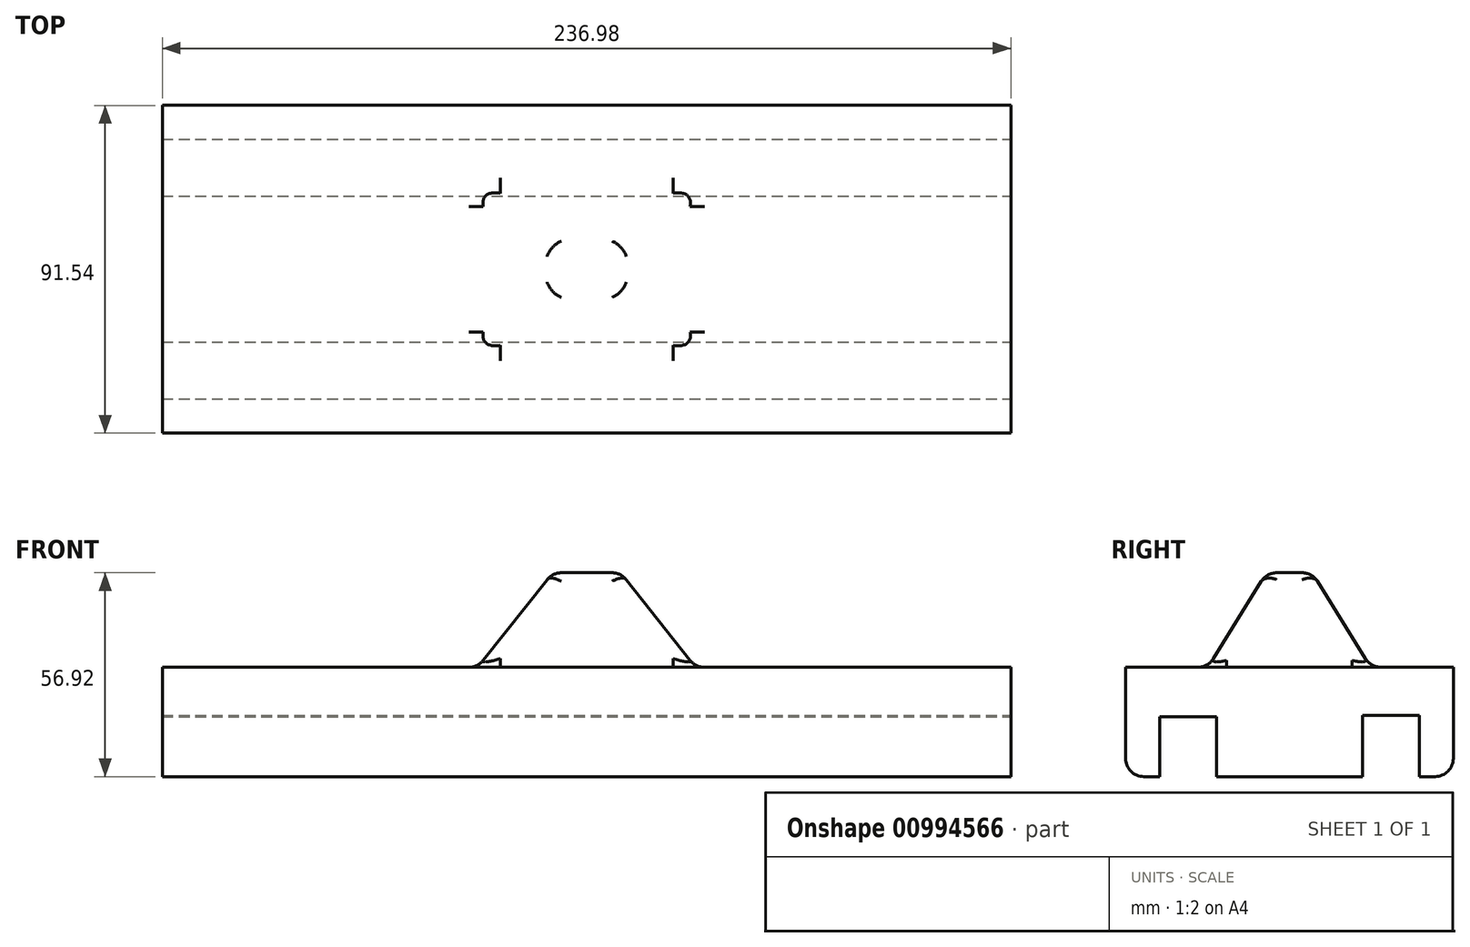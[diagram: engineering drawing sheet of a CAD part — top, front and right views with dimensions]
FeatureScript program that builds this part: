
annotation { "Feature Type Name" : "Feature", "Feature Type Description" : "" }
export const myFeature = defineFeature(function(context is Context, id is Id, definition is map)
    precondition{}
    {
        {
            var Q0;
            Q0=qCreatedBy(makeId("Front.planeOp"),FACE);
            var sketch = newSketch(context, id + "F0", { "sketchPlane" : qUnion([Q0])});
            skLineSegment(sketch, "E0.bottom", {"start": v(0, 0) * mm, "end": v(118.5, 0) * mm});
            skLineSegment(sketch, "E0.top", {"start": v(30.4, 30.53) * mm, "end": v(118.5, 30.53) * mm});
            skLineSegment(sketch, "E0.left", {"start": v(0, 0) * mm, "end": v(0, 30.53) * mm});
            skLineSegment(sketch, "E0.right", {"start": v(118.5, 0) * mm, "end": v(118.5, 30.53) * mm});
            skLineSegment(sketch, "E1", {"start": v(0, 30.53) * mm, "end": v(0, 56.92) * mm});
            skLineSegment(sketch, "E2", {"start": v(0, 56.92) * mm, "end": v(9.52, 56.92) * mm});
            skLineSegment(sketch, "E3", {"start": v(9.52, 56.92) * mm, "end": v(30.4, 30.53) * mm});
            skSolve(sketch);
        }
        {
            var Q0;
            Q0 = qSketchRegion(id + "F0", true);
            extrude(context, id + "F1", {"entities" : qUnion([Q0]), "depth" : 91.54 * mm, "offsetDistance" : 25.4 * mm, "symmetric" : true});
        }
        {
            var Q0;
            Q0=makeQuery(id+"F1.opExtrude","SWEPT_BODY",BODY,{"disambiguationData":[OSD([sQuery(id+"F0.wireOp",EDGE,"E0.bottom"),sQuery(id+"F0.wireOp",EDGE,"E0.top"),sQuery(id+"F0.wireOp",EDGE,"E0.left"),sQuery(id+"F0.wireOp",EDGE,"E0.right"),sQuery(id+"F0.wireOp",EDGE,"E1"),sQuery(id+"F0.wireOp",EDGE,"E2"),sQuery(id+"F0.wireOp",EDGE,"E3")])]});
            var Q1;
            Q1=makeQuery(id+"F1.opExtrude","SWEPT_FACE",FACE,{"disambiguationData":[OSD([sQuery(id+"F0.wireOp",EDGE,"E0.left"),sQuery(id+"F0.wireOp",EDGE,"E1")])]});
            mirror(context, id + "F2", {"operationType" : NewBodyOperationType.ADD, "entities" : qUnion([Q0]), "mirrorPlane" : qUnion([Q1])});
        }
        {
            var Q0;
            Q0=makeQuery(id+"F1.opExtrude","SWEPT_FACE",FACE,{"disambiguationData":[OSD([sQuery(id+"F0.wireOp",EDGE,"E0.right")])]});
            var sketch = newSketch(context, id + "F3", { "sketchPlane" : qUnion([Q0])});
            skLineSegment(sketch, "E4", {"start": v(0, 56.58) * mm, "end": v(0, 30.53) * mm});
            skLineSegment(sketch, "E5", {"start": v(22.72, 30.53) * mm, "end": v(6.35, 56.92) * mm});
            skLineSegment(sketch, "E6", {"start": v(6.35, 56.92) * mm, "end": v(45.77, 56.92) * mm});
            skLineSegment(sketch, "E7", {"start": v(45.77, 56.92) * mm, "end": v(45.77, 30.53) * mm});
            skLineSegment(sketch, "E8", {"start": v(45.77, 30.53) * mm, "end": v(22.72, 30.53) * mm});
            skLineSegment(sketch, "E9.MirrorCS", {"start": v(-45.77, 30.53) * mm, "end": v(-22.72, 30.53) * mm});
            skLineSegment(sketch, "E10.MirrorCS", {"start": v(-6.35, 56.92) * mm, "end": v(-45.77, 56.92) * mm});
            skLineSegment(sketch, "E11.MirrorCS", {"start": v(-22.72, 30.53) * mm, "end": v(-6.35, 56.92) * mm});
            skLineSegment(sketch, "E12.MirrorCS", {"start": v(-45.77, 56.92) * mm, "end": v(-45.77, 30.53) * mm});
            skSolve(sketch);
        }
        {
            var Q0;
            Q0 = qSketchRegion(id + "F3", true);
            extrude(context, id + "F4", {"entities" : qUnion([Q0]), "operationType" : NewBodyOperationType.REMOVE, "endBound" : BoundingType.THROUGH_ALL, "oppositeDirection" : true, "depth" : 25.4 * mm, "offsetDistance" : 25.4 * mm});
        }
        {
            var Q0;
            Q0=makeQuery(id+"F1.opExtrude","SWEPT_FACE",FACE,{"disambiguationData":[OSD([sQuery(id+"F0.wireOp",EDGE,"E0.right")])]});
            var sketch = newSketch(context, id + "F5", { "sketchPlane" : qUnion([Q0])});
            skLineSegment(sketch, "E13.bottom", {"start": v(-36.25, 0) * mm, "end": v(-20.37, 0) * mm});
            skLineSegment(sketch, "E13.top", {"start": v(-36.25, 16.66) * mm, "end": v(-20.37, 16.66) * mm});
            skLineSegment(sketch, "E13.left", {"start": v(-36.25, 0) * mm, "end": v(-36.25, 16.66) * mm});
            skLineSegment(sketch, "E13.right", {"start": v(-20.37, 0) * mm, "end": v(-20.37, 16.66) * mm});
            skSolve(sketch);
        }
        {
            var Q0;
            Q0 = qSketchRegion(id + "F5", true);
            extrude(context, id + "F6", {"entities" : qUnion([Q0]), "operationType" : NewBodyOperationType.REMOVE, "endBound" : BoundingType.UP_TO_NEXT, "oppositeDirection" : true, "depth" : 116.33 * mm, "offsetDistance" : 25.4 * mm, "hasSecondDirection" : true, "secondDirectionOppositeDirection" : false, "secondDirectionDepth" : 25.4 * mm});
        }
        {
            var Q0;
            Q0=makeQuery(id+"F1.opExtrude","SWEPT_FACE",FACE,{"disambiguationData":[OSD([sQuery(id+"F0.wireOp",EDGE,"E0.right")])]});
            var sketch = newSketch(context, id + "F7", { "sketchPlane" : qUnion([Q0])});
            skLineSegment(sketch, "E14.bottom", {"start": v(36.25, 0) * mm, "end": v(20.37, 0) * mm});
            skLineSegment(sketch, "E14.top", {"start": v(36.25, 17.1) * mm, "end": v(20.37, 17.1) * mm});
            skLineSegment(sketch, "E14.left", {"start": v(36.25, 0) * mm, "end": v(36.25, 17.1) * mm});
            skLineSegment(sketch, "E14.right", {"start": v(20.37, 0) * mm, "end": v(20.37, 17.1) * mm});
            skSolve(sketch);
        }
        {
            var Q0;
            Q0 = qSketchRegion(id + "F7", true);
            extrude(context, id + "F8", {"entities" : qUnion([Q0]), "operationType" : NewBodyOperationType.REMOVE, "endBound" : BoundingType.UP_TO_NEXT, "oppositeDirection" : true, "depth" : 25.4 * mm, "offsetDistance" : 25.4 * mm});
        }
        {
            var Q0;
            {var subQ0=makeQuery(id+"F1.opExtrude","SWEPT_FACE",FACE,{"disambiguationData":[OSD([sQuery(id+"F0.wireOp",EDGE,"E2")])]});Q0=makeQuery(id+"F2.boolean.opBoolean","MERGE",FACE,{"derivedFrom":[subQ0,makeQuery(id+"F2.opPattern","COPY",FACE,{"derivedFrom":subQ0,"instanceName":"1"})]});}
            fillet(context, id + "F9", {"entities" : qUnion([Q0]), "radius" : 5.08 * mm, "tangentPropagation" : true, "allowEdgeOverflow" : false});
        }
        {
            var Q0;
            {var subQ0=makeQuery(id+"F1.opExtrude","CAP_EDGE",EDGE,{"disambiguationData":[OSD([sQuery(id+"F0.wireOp",EDGE,"E0.bottom")])],"isStart":true});Q0=makeQuery(id+"F2.boolean.opBoolean","MERGE",EDGE,{"derivedFrom":[subQ0,makeQuery(id+"F2.opPattern","COPY",EDGE,{"derivedFrom":subQ0,"instanceName":"1"})]});}
            var Q1;
            {var subQ0=makeQuery(id+"F1.opExtrude","CAP_EDGE",EDGE,{"disambiguationData":[OSD([sQuery(id+"F0.wireOp",EDGE,"E0.bottom")])],"isStart":false});Q1=makeQuery(id+"F2.boolean.opBoolean","MERGE",EDGE,{"derivedFrom":[subQ0,makeQuery(id+"F2.opPattern","COPY",EDGE,{"derivedFrom":subQ0,"instanceName":"1"})]});}
            fillet(context, id + "F10", {"entities" : qUnion([Q0, Q1]), "radius" : 5.08 * mm, "tangentPropagation" : true, "allowEdgeOverflow" : false});
        }
        {
            var Q0;
            Q0=makeQuery(id+"F1.opExtrude","SWEPT_EDGE",EDGE,{"disambiguationData":[OSD([sQuery(id+"F0.wireOp",EDGE,"E0.top"),sQuery(id+"F0.wireOp",EDGE,"E3")])]});
            var Q1;
            Q1=makeQuery(id+"F4.boolean.opBoolean","INTERSECT",EDGE,{"derivedFrom":[makeQuery(id+"F1.opExtrude","SWEPT_FACE",FACE,{"disambiguationData":[OSD([sQuery(id+"F0.wireOp",EDGE,"E3")])]}),makeQuery(id+"F4.opExtrude","SWEPT_FACE",FACE,{"disambiguationData":[OSD([sQuery(id+"F3.wireOp",EDGE,"E11.MirrorCS")])]})]});
            var Q2;
            Q2=makeQuery(id+"F4.boolean.opBoolean","COPY",EDGE,{"derivedFrom":makeQuery(id+"F4.opExtrude","SWEPT_EDGE",EDGE,{"disambiguationData":[OSD([sQuery(id+"F0.wireOp",EDGE,"E0.top"),sQuery(id+"F0.wireOp",EDGE,"E0.right"),sQuery(id+"F3.wireOp",EDGE,"E9.MirrorCS"),sQuery(id+"F3.wireOp",EDGE,"E11.MirrorCS")])]})});
            var Q3;
            Q3=makeQuery(id+"F4.boolean.opBoolean","INTERSECT",EDGE,{"derivedFrom":[makeQuery(id+"F1.opExtrude","SWEPT_FACE",FACE,{"disambiguationData":[OSD([sQuery(id+"F0.wireOp",EDGE,"E3")])]}),makeQuery(id+"F4.opExtrude","SWEPT_FACE",FACE,{"disambiguationData":[OSD([sQuery(id+"F3.wireOp",EDGE,"E5")])]})]});
            var Q4;
            Q4=makeQuery(id+"F4.boolean.opBoolean","INTERSECT",EDGE,{"derivedFrom":[makeQuery(id+"F2.opPattern","COPY",FACE,{"derivedFrom":makeQuery(id+"F1.opExtrude","SWEPT_FACE",FACE,{"disambiguationData":[OSD([sQuery(id+"F0.wireOp",EDGE,"E3")])]}),"instanceName":"1"}),makeQuery(id+"F4.opExtrude","SWEPT_FACE",FACE,{"disambiguationData":[OSD([sQuery(id+"F3.wireOp",EDGE,"E11.MirrorCS")])]})]});
            var Q5;
            Q5=makeQuery(id+"F2.opPattern","COPY",EDGE,{"derivedFrom":makeQuery(id+"F1.opExtrude","SWEPT_EDGE",EDGE,{"disambiguationData":[OSD([sQuery(id+"F0.wireOp",EDGE,"E0.top"),sQuery(id+"F0.wireOp",EDGE,"E3")])]}),"instanceName":"1"});
            var Q6;
            Q6=makeQuery(id+"F4.boolean.opBoolean","INTERSECT",EDGE,{"derivedFrom":[makeQuery(id+"F2.opPattern","COPY",FACE,{"derivedFrom":makeQuery(id+"F1.opExtrude","SWEPT_FACE",FACE,{"disambiguationData":[OSD([sQuery(id+"F0.wireOp",EDGE,"E3")])]}),"instanceName":"1"}),makeQuery(id+"F4.opExtrude","SWEPT_FACE",FACE,{"disambiguationData":[OSD([sQuery(id+"F3.wireOp",EDGE,"E5")])]})]});
            var Q7;
            Q7=makeQuery(id+"F4.boolean.opBoolean","COPY",EDGE,{"derivedFrom":makeQuery(id+"F4.opExtrude","SWEPT_EDGE",EDGE,{"disambiguationData":[OSD([sQuery(id+"F0.wireOp",EDGE,"E0.top"),sQuery(id+"F0.wireOp",EDGE,"E0.right"),sQuery(id+"F3.wireOp",EDGE,"E5"),sQuery(id+"F3.wireOp",EDGE,"E8")])]})});
            fillet(context, id + "F11", {"entities" : qUnion([Q0, Q1, Q2, Q3, Q4, Q5, Q6, Q7]), "radius" : 5.08 * mm, "tangentPropagation" : true, "allowEdgeOverflow" : false});
        }
    });
